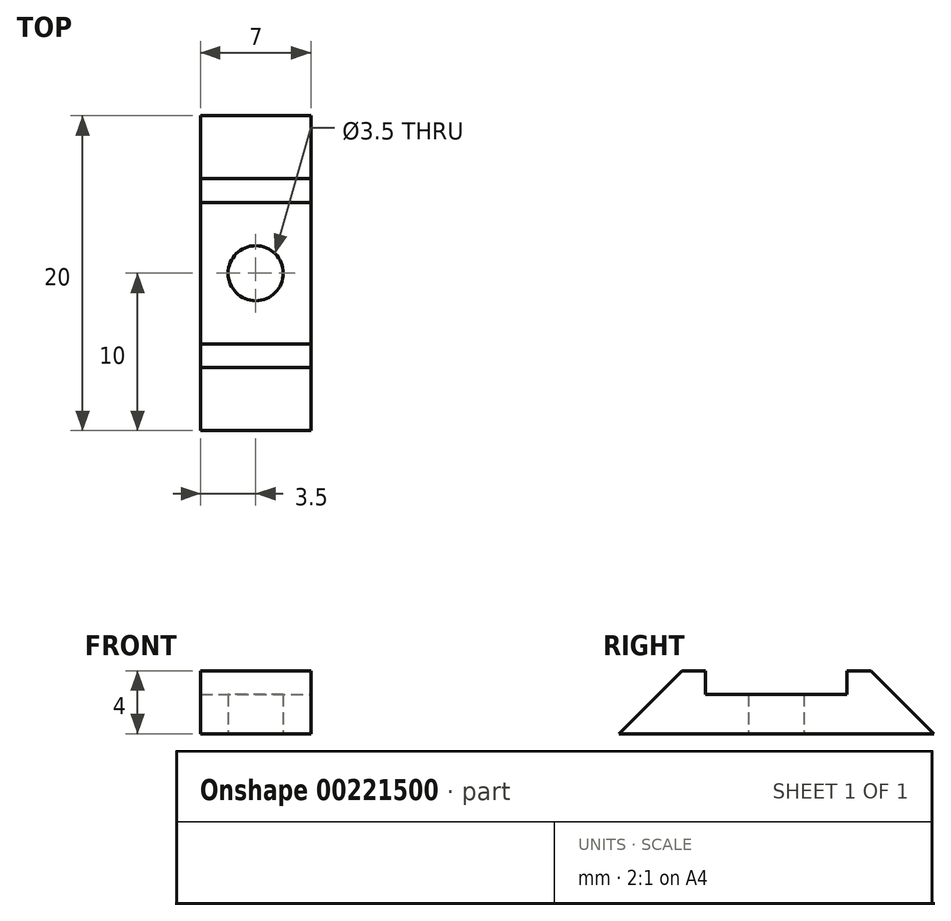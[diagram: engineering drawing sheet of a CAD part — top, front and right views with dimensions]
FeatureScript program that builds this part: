
annotation { "Feature Type Name" : "Feature", "Feature Type Description" : "" }
export const myFeature = defineFeature(function(context is Context, id is Id, definition is map)
    precondition{}
    {
        {
            var Q0;
            Q0=qCreatedBy(makeId("Top.planeOp"),FACE);
            var sketch = newSketch(context, id + "F0", { "sketchPlane" : qUnion([Q0])});
            skCircle(sketch, "E0", {"center": v(0, 0) * mm, "radius": 1.75 * mm});
            skLineSegment(sketch, "E1.bottom", {"start": v(-3.5, 10) * mm, "end": v(3.5, 10) * mm});
            skLineSegment(sketch, "E1.top", {"start": v(-3.5, -10) * mm, "end": v(3.5, -10) * mm});
            skLineSegment(sketch, "E1.left", {"start": v(-3.5, 10) * mm, "end": v(-3.5, -10) * mm});
            skLineSegment(sketch, "E1.right", {"start": v(3.5, 10) * mm, "end": v(3.5, -10) * mm});
            skPoint(sketch, "E2", {"position": v(0, 10) * mm});
            skPoint(sketch, "E3", {"position": v(3.5, 0) * mm});
            skSolve(sketch);
        }
        {
            var Q0;
            Q0=makeQuery(id+"F0.imprint","IMPRINT",FACE,{"disambiguationData":[TD([[makeQuery(id+"F0.imprint","IMPRINT",EDGE,{"derivedFrom":sQuery(id+"F0.wireOp",EDGE,"E0")}),-1.0]])]});
            extrude(context, id + "F1", {"entities" : qUnion([Q0]), "depth" : 2.5 * mm});
        }
        {
            var Q0;
            Q0=makeQuery(id+"F1.opExtrude","CAP_FACE",FACE,{"disambiguationData":[OSD([sQuery(id+"F0.wireOp",EDGE,"E0"),sQuery(id+"F0.wireOp",EDGE,"E1.bottom"),sQuery(id+"F0.wireOp",EDGE,"E1.top"),sQuery(id+"F0.wireOp",EDGE,"E1.left"),sQuery(id+"F0.wireOp",EDGE,"E1.right")])],"isStart":false});
            var sketch = newSketch(context, id + "F2", { "sketchPlane" : qUnion([Q0])});
            skLineSegment(sketch, "E4.bottom", {"start": v(-3.5, 10) * mm, "end": v(3.5, 10) * mm});
            skLineSegment(sketch, "E4.top", {"start": v(-3.5, 4.5) * mm, "end": v(3.5, 4.5) * mm});
            skLineSegment(sketch, "E4.left", {"start": v(-3.5, 10) * mm, "end": v(-3.5, 4.5) * mm});
            skLineSegment(sketch, "E4.right", {"start": v(3.5, 10) * mm, "end": v(3.5, 4.5) * mm});
            skLineSegment(sketch, "E5.bottom", {"start": v(-3.5, -10) * mm, "end": v(3.5, -10) * mm});
            skLineSegment(sketch, "E5.top", {"start": v(-3.5, -4.5) * mm, "end": v(3.5, -4.5) * mm});
            skLineSegment(sketch, "E5.left", {"start": v(-3.5, -10) * mm, "end": v(-3.5, -4.5) * mm});
            skLineSegment(sketch, "E5.right", {"start": v(3.5, -10) * mm, "end": v(3.5, -4.5) * mm});
            skSolve(sketch);
        }
        {
            var Q0;
            Q0=makeQuery(id+"F2.imprint","IMPRINT",FACE,{"disambiguationData":[TD([[makeQuery(id+"F2.imprint","IMPRINT",EDGE,{"derivedFrom":sQuery(id+"F2.wireOp",EDGE,"E4.bottom")}),-1.0]])]});
            var Q1;
            Q1=makeQuery(id+"F2.imprint","IMPRINT",FACE,{"disambiguationData":[TD([[makeQuery(id+"F2.imprint","IMPRINT",EDGE,{"derivedFrom":sQuery(id+"F2.wireOp",EDGE,"E5.bottom")}),1.0]])]});
            extrude(context, id + "F3", {"entities" : qUnion([Q0, Q1]), "operationType" : NewBodyOperationType.ADD, "depth" : 1.5 * mm});
        }
        {
            var Q0;
            Q0=makeQuery(id+"F3.opExtrude","CAP_EDGE",EDGE,{"disambiguationData":[OSD([sQuery(id+"F2.wireOp",EDGE,"E4.bottom")])],"isStart":false});
            var Q1;
            Q1=makeQuery(id+"F3.opExtrude","CAP_EDGE",EDGE,{"disambiguationData":[OSD([sQuery(id+"F2.wireOp",EDGE,"E5.bottom")])],"isStart":false});
            chamfer(context, id + "F4", {"entities" : qUnion([Q0, Q1]), "width" : 4 * mm, "tangentPropagation" : true});
        }
    });
